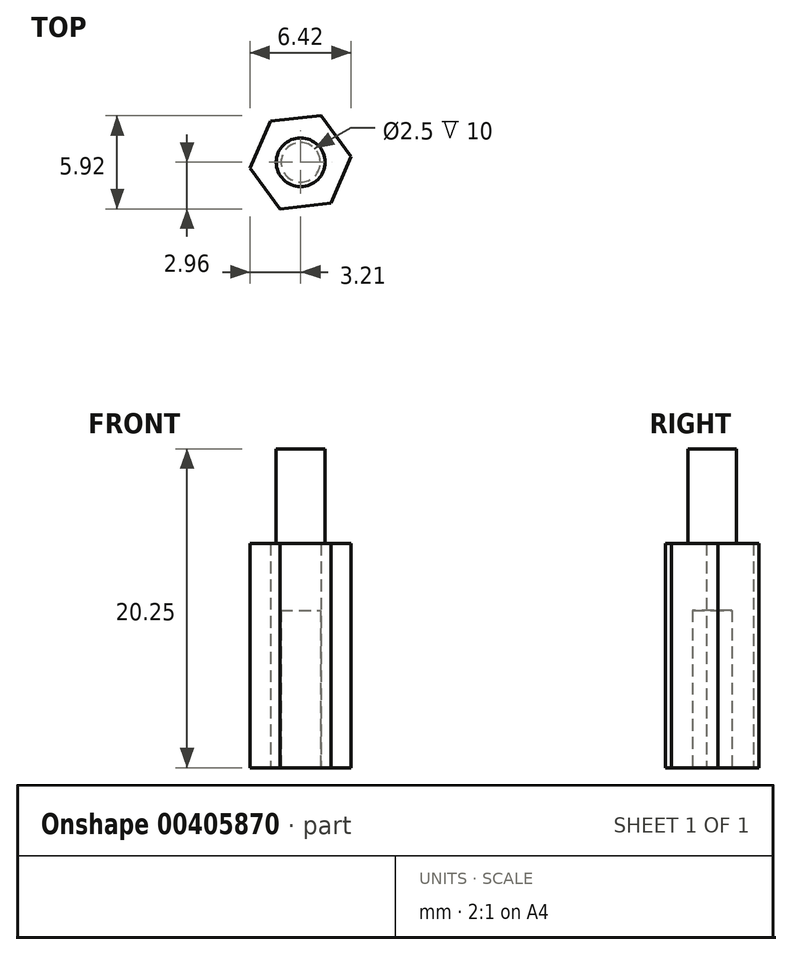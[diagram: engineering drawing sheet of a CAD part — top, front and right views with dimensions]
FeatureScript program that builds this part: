
annotation { "Feature Type Name" : "Feature", "Feature Type Description" : "" }
export const myFeature = defineFeature(function(context is Context, id is Id, definition is map)
    precondition{}
    {
        {
            var Q0;
            Q0=qCreatedBy(makeId("Top.planeOp"),FACE);
            var sketch = newSketch(context, id + "F0", { "sketchPlane" : qUnion([Q0])});
            skCircle(sketch, "E0.cCircle", {"center": v(0, 0) * mm, "radius": 2.8 * mm, "construction": true});
            skLineSegment(sketch, "E0.0", {"start": v(-3.21, -0.36) * mm, "end": v(-1.92, 2.6) * mm});
            skLineSegment(sketch, "E0.1", {"start": v(-1.92, 2.6) * mm, "end": v(1.3, 2.96) * mm});
            skLineSegment(sketch, "E0.2", {"start": v(1.3, 2.96) * mm, "end": v(3.21, 0.36) * mm});
            skLineSegment(sketch, "E0.3", {"start": v(3.21, 0.36) * mm, "end": v(1.92, -2.6) * mm});
            skLineSegment(sketch, "E0.4", {"start": v(1.92, -2.6) * mm, "end": v(-1.3, -2.96) * mm});
            skLineSegment(sketch, "E0.5", {"start": v(-1.3, -2.96) * mm, "end": v(-3.21, -0.36) * mm});
            skPoint(sketch, "E0.0.midPoint", {"position": v(-2.57, 1.12) * mm});
            skSolve(sketch);
        }
        {
            var Q0;
            Q0 = qSketchRegion(id + "F0", true);
            extrude(context, id + "F1", {"entities" : qUnion([Q0]), "depth" : 14.25 * mm});
        }
        {
            var Q0;
            Q0=makeQuery(id+"F1.opExtrude","CAP_FACE",FACE,{"disambiguationData":[OSD([sQuery(id+"F0.wireOp",EDGE,"E0.0"),sQuery(id+"F0.wireOp",EDGE,"E0.1"),sQuery(id+"F0.wireOp",EDGE,"E0.2"),sQuery(id+"F0.wireOp",EDGE,"E0.3"),sQuery(id+"F0.wireOp",EDGE,"E0.4"),sQuery(id+"F0.wireOp",EDGE,"E0.5")])],"isStart":true});
            var sketch = newSketch(context, id + "F2", { "sketchPlane" : qUnion([Q0])});
            skCircle(sketch, "E1", {"center": v(0, 0) * mm, "radius": 1.25 * mm});
            skSolve(sketch);
        }
        {
            var Q0;
            Q0 = qSketchRegion(id + "F2", true);
            extrude(context, id + "F3", {"entities" : qUnion([Q0]), "operationType" : NewBodyOperationType.REMOVE, "oppositeDirection" : true, "depth" : 10 * mm});
        }
        {
            var Q0;
            Q0=makeQuery(id+"F1.opExtrude","CAP_FACE",FACE,{"disambiguationData":[OSD([sQuery(id+"F0.wireOp",EDGE,"E0.0"),sQuery(id+"F0.wireOp",EDGE,"E0.1"),sQuery(id+"F0.wireOp",EDGE,"E0.2"),sQuery(id+"F0.wireOp",EDGE,"E0.3"),sQuery(id+"F0.wireOp",EDGE,"E0.4"),sQuery(id+"F0.wireOp",EDGE,"E0.5")])],"isStart":false});
            var sketch = newSketch(context, id + "F4", { "sketchPlane" : qUnion([Q0])});
            skCircle(sketch, "E2", {"center": v(0, 0) * mm, "radius": 1.55 * mm});
            skSolve(sketch);
        }
        {
            var Q0;
            Q0 = qSketchRegion(id + "F4", true);
            extrude(context, id + "F5", {"entities" : qUnion([Q0]), "operationType" : NewBodyOperationType.ADD, "depth" : 6 * mm});
        }
    });
